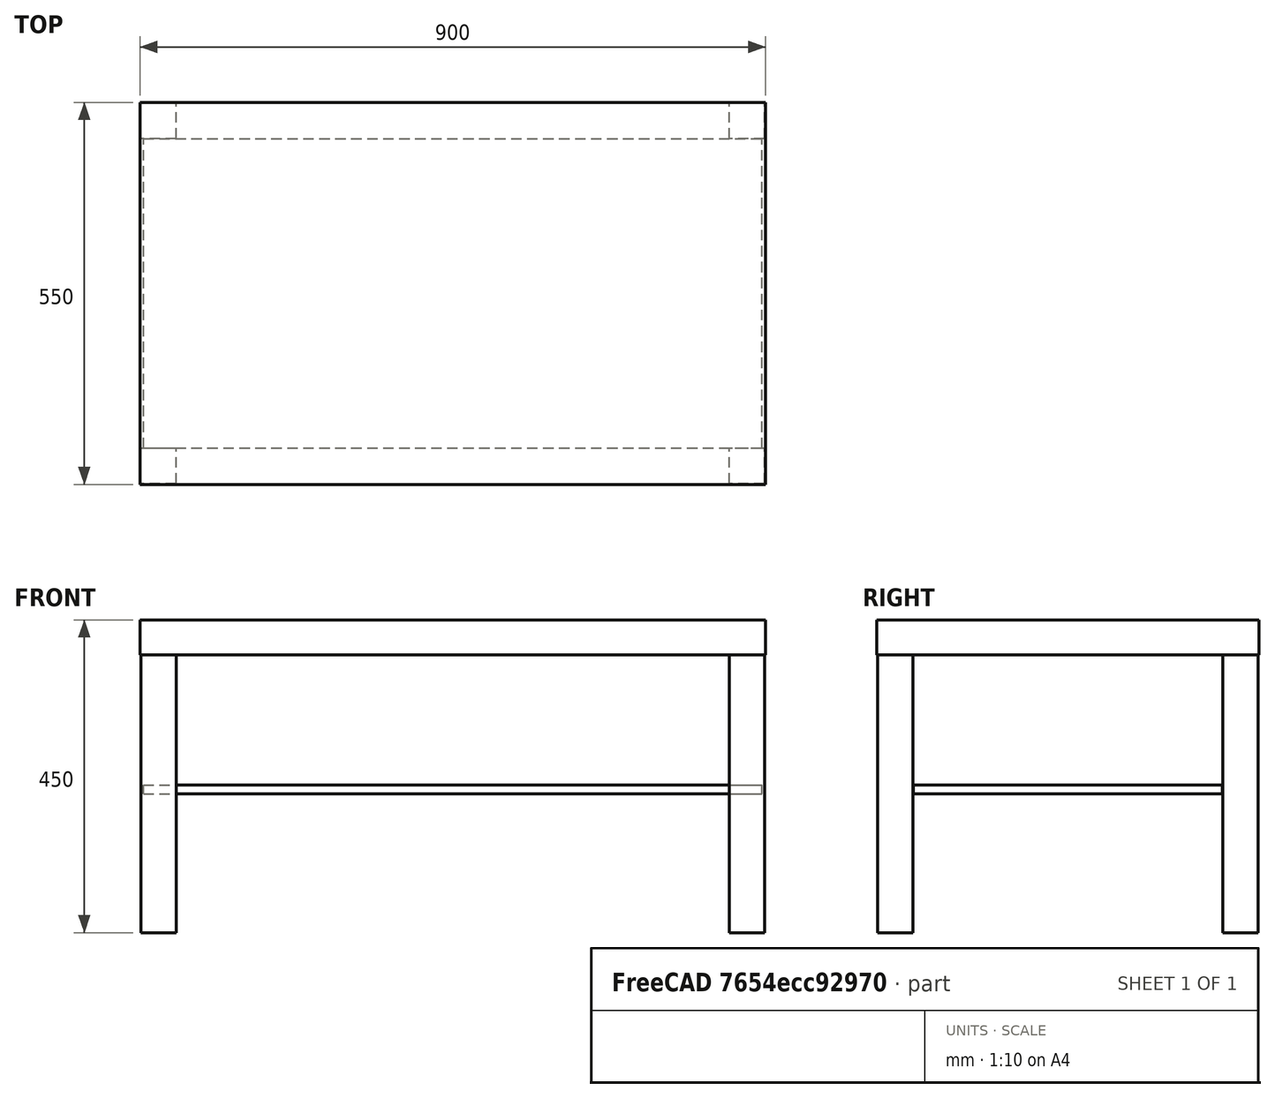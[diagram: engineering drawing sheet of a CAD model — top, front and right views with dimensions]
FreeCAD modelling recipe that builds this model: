
FCSTD DOCUMENT
Label: IKEA_Lack_900_550_450
objects: Part::Box×6, Part::MultiFuse×2
note: 8 computed .brp shape members not serialized (recipe doc carries the construction recipe); baked Part::Feature solids carry a one-line shape summary decoded from their .brp

FEATURE [Part::Box] Box
  Height = 50
  Length = 900
  Placement = pos=(0,0,400) rot=(0,0,1;0rad)
  Width = 550
FEATURE [Part::Box] Box001
  Height = 405
  Length = 50.5
  Placement = pos=(1.5,1.5,0) rot=(0,0,1;0rad)
  Width = 50.5
FEATURE [Part::Box] Box002
  Height = 405
  Length = 50.5
  Placement = pos=(1.5,498,0) rot=(0,0,1;0rad)
  Width = 50.5
FEATURE [Part::Box] Box003
  Height = 405
  Length = 50.5
  Placement = pos=(848,1.5,0) rot=(0,0,1;0rad)
  Width = 50.5
FEATURE [Part::Box] Box004
  Height = 405
  Length = 50.5
  Placement = pos=(848,498,0) rot=(0,0,1;0rad)
  Width = 50.5
FEATURE [Part::MultiFuse] Fusion
  Shapes = -> [Box,Box002,Box003,Box004,Box001]
FEATURE [Part::Box] Box005
  Height = 12.2
  Length = 890
  Placement = pos=(5,52.5,200) rot=(0,0,1;0rad)
  Width = 445
FEATURE [Part::MultiFuse] Fusion001  label="ikea_lack"
  Shapes = -> [Fusion,Box005]
